# Revit family: Drain_Roof-Jay R.Smith-Round-Type-1830_Series
name_source: partatom
category: Plumbing Fixtures
units: mm (PartAtom-declared; Revit-internal decimal feet)

## family parameters
Always vertical = No
Cut with Voids When Loaded = No
OmniClass Number = 23.70.50.21.24.11
OmniClass Title = Roof Waste Water Drains
Part Type = Normal
Room Calculation Point = No
Round Connector Dimension = Use Diameter
Shared = Yes
Work Plane-Based = Yes

## types (6) — shared parameters
AD - Aluminum Dome = No
Assembly Code = D2040200
C2 - Secondary Flashing Clamp = No
CID - Cast Iron Dome = No
CIDG - Galvanized Cast Iron Dome = No
CW Connection = No
Deck Plate Material = Metal-Jay R Smith - Stainless Steel
Default Elevation = 0"
Description = Roof and Overflow Drain with Deck-Top Mounting Plate
Diameter = 15 1/4"
Dome Material = Plastic-Jay R Smith-Polyethylene
Drain Material = Cast Iron-Jay R Smith-Duco Coated
G - Galvanized Cast Iron Body & Collar = No
HW Connection = No
Height = 10 1/4"
Installation Type = Roof Mounted
L - Speedi-Set Service Weight = No
LXH - Speedi-Set Extra Heavy = No
Length = 32"
Manufacturer = Jay R. Smith
Product Documentation Link = https://www.jrsmith.com
Product Page URL = https://www.jrsmith.com
RBD - Rough Bronze Dome = No
Standpipe Material = Polymer - Jay R Smith - PVC
T - Threaded Outlet = No
U - Vandal Proof Dome = No
URL = http://www.jrsmith.com
Vent Connection = No
Waste Connection = Yes
Width = 16"

## per-type parameters (varying)
| type | Connection Description 1 | Connection Description 2 | Connection Radius | Connection Size |
| 1830C02 | 2" Caulk Outlet Connection 1 | 2" Caulk Outlet Connection 2 | 1" | 2" |
| 1830C03 | 3" Caulk Outlet Connection 1 | 3" Caulk Outlet Connection 2 | 1 1/2" | 3" |
| 1830C04 | 4" Caulk Outlet Connection 1 | 4" Caulk Outlet Connection 2 | 2" | 4" |
| 1830Y03 | 3" No-HUB Connection 1 | 3" No-HUB Connection 2 | 1 1/2" | 3" |
| 1830Y02 | 2" No-HUB Connection 1 | 2" No-HUB Connection 2 | 1" | 2" |
| 1830Y04 | 4" No-HUB Connection 1 | 4" No-HUB Connection 2 | 2" | 4" |

note: column(s) folded — value = type name in every type: Model

## geometry (parser evidence)
native form markers: Sweep x2
no freeform markers — native parametric forms only
